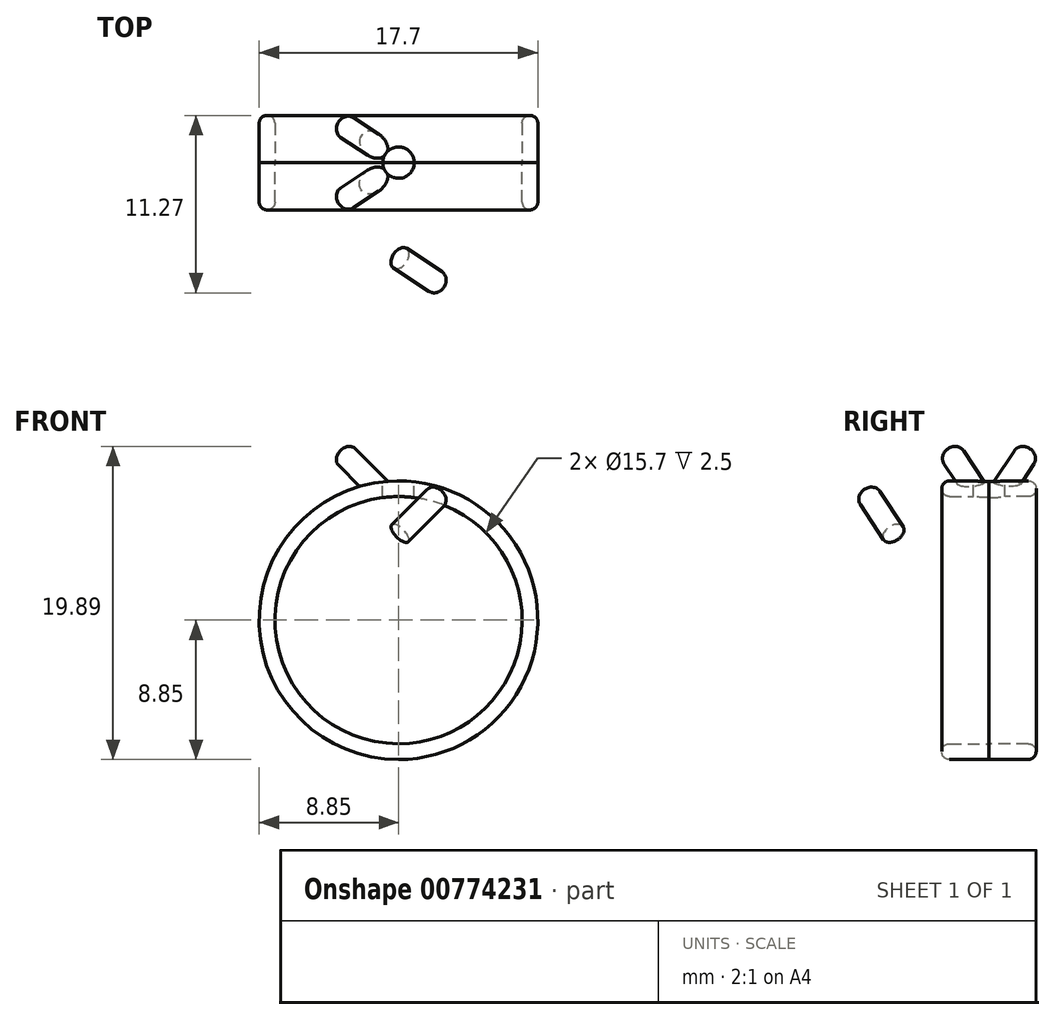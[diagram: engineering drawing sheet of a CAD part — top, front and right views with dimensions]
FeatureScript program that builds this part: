
annotation { "Feature Type Name" : "Feature", "Feature Type Description" : "" }
export const myFeature = defineFeature(function(context is Context, id is Id, definition is map)
    precondition{}
    {
        {
            var Q0;
            Q0=qCreatedBy(makeId("Front.planeOp"),FACE);
            var sketch = newSketch(context, id + "F0", { "sketchPlane" : qUnion([Q0])});
            skCircle(sketch, "E0", {"center": v(0, 0) * mm, "radius": 7.85 * mm});
            skCircle(sketch, "E1", {"center": v(0, 0) * mm, "radius": 8.85 * mm});
            skSolve(sketch);
        }
        {
            var Q0;
            Q0 = qSketchRegion(id + "F0", true);
            extrude(context, id + "F1", {"entities" : qUnion([Q0]), "depth" : 3 * mm, "offsetDistance" : 25 * mm});
        }
        {
            var Q0;
            Q0=makeQuery(id+"F1.opExtrude","CAP_FACE",FACE,{"disambiguationData":[OSD([sQuery(id+"F0.wireOp",EDGE,"E0"),sQuery(id+"F0.wireOp",EDGE,"E1")])],"isStart":false});
            cPlane(context, id + "F2", {"entities" : qUnion([Q0]), "cplaneType" : CPlaneType.OFFSET, "offset" : 2.25 * mm, "oppositeDirection" : true, "width" : 150 * mm, "height" : 150 * mm});
        }
        {
            var Q0;
            Q0=qCreatedBy(id+"F2.planeOp",FACE);
            var sketch = newSketch(context, id + "F3", { "sketchPlane" : qUnion([Q0])});
            skLineSegment(sketch, "E2", {"start": v(0, 15) * mm, "end": v(0, -15.53) * mm, "construction": true});
            skLineSegment(sketch, "E3", {"start": v(1, 8.09) * mm, "end": v(1, 8.1) * mm});
            skLineSegment(sketch, "E4", {"start": v(-1, 8.09) * mm, "end": v(-1, 8.1) * mm});
            skSolve(sketch);
        }
        {
            var Q0;
            Q0=sQuery(id+"F3.wireOp",EDGE,"E3");
            cPlane(context, id + "F4", {"entities" : qUnion([Q0]), "cplaneType" : CPlaneType.LINE_ANGLE, "offset" : 25 * mm, "angle" : 90 * degree, "oppositeDirection" : true, "width" : 150 * mm, "height" : 150 * mm});
        }
        {
            var Q0;
            Q0=sQuery(id+"F3.wireOp",EDGE,"E4");
            cPlane(context, id + "F5", {"entities" : qUnion([Q0]), "cplaneType" : CPlaneType.LINE_ANGLE, "offset" : 25 * mm, "angle" : 90 * degree, "width" : 150 * mm, "height" : 150 * mm});
        }
        {
            var Q0;
            Q0=qCreatedBy(id+"F4.planeOp",FACE);
            var sketch = newSketch(context, id + "F6", { "sketchPlane" : qUnion([Q0])});
            skLineSegment(sketch, "E5", {"start": v(-0.75, 6.44) * mm, "end": v(-0.75, 6.45) * mm});
            skLineSegment(sketch, "E6", {"start": v(-0.75, 6.45) * mm, "end": v(-2.44, 10.07) * mm});
            skSolve(sketch);
        }
        {
            var Q0;
            Q0=qCreatedBy(id+"F5.planeOp",FACE);
            var sketch = newSketch(context, id + "F7", { "sketchPlane" : qUnion([Q0])});
            skLineSegment(sketch, "E7", {"start": v(-0.75, 6.44) * mm, "end": v(-0.75, 6.45) * mm});
            skLineSegment(sketch, "E8", {"start": v(-0.75, 6.45) * mm, "end": v(-2.44, 10.07) * mm});
            skSolve(sketch);
        }
        {
            var Q0;
            Q0=sQuery(id+"F6.wireOp",VERTEX,"E6.end");
            var Q1;
            Q1=sQuery(id+"F6.wireOp",EDGE,"E6");
            cPlane(context, id + "F8", {"entities" : qUnion([Q0, Q1]), "cplaneType" : CPlaneType.LINE_POINT, "offset" : 25 * mm, "width" : 150 * mm, "height" : 150 * mm});
        }
        {
            var Q0;
            Q0=sQuery(id+"F7.wireOp",VERTEX,"E8.end");
            var Q1;
            Q1=sQuery(id+"F7.wireOp",EDGE,"E8");
            cPlane(context, id + "F9", {"entities" : qUnion([Q0, Q1]), "cplaneType" : CPlaneType.LINE_POINT, "offset" : 25 * mm, "width" : 150 * mm, "height" : 150 * mm});
        }
        {
            var Q0;
            Q0=qCreatedBy(id+"F8.planeOp",FACE);
            var sketch = newSketch(context, id + "F10", { "sketchPlane" : qUnion([Q0])});
            skCircle(sketch, "E9", {"center": v(-3.82, 3.83) * mm, "radius": 0.75 * mm});
            skSolve(sketch);
        }
        {
            var Q0;
            Q0=qCreatedBy(id+"F9.planeOp",FACE);
            var sketch = newSketch(context, id + "F11", { "sketchPlane" : qUnion([Q0])});
            skCircle(sketch, "E10", {"center": v(-2.04, 5.01) * mm, "radius": 0.75 * mm});
            skSolve(sketch);
        }
        {
            var Q0;
            Q0=makeQuery(id+"F10.imprint","IMPRINT",FACE,{"disambiguationData":[TD([[makeQuery(id+"F10.imprint","IMPRINT",EDGE,{"derivedFrom":sQuery(id+"F10.wireOp",EDGE,"E9")}),1.0]])]});
            var Q1;
            Q1=sQuery(id+"F6.wireOp",EDGE,"E6");
            sweep(context, id + "F12", {"operationType" : NewBodyOperationType.ADD, "profiles" : qUnion([Q0]), "path" : qUnion([Q1])});
        }
        {
            var Q0;
            Q0=makeQuery(id+"F11.imprint","IMPRINT",FACE,{"disambiguationData":[TD([[makeQuery(id+"F11.imprint","IMPRINT",EDGE,{"derivedFrom":sQuery(id+"F11.wireOp",EDGE,"E10")}),1.0]])]});
            var Q1;
            Q1=sQuery(id+"F7.wireOp",EDGE,"E8");
            sweep(context, id + "F13", {"operationType" : NewBodyOperationType.ADD, "profiles" : qUnion([Q0]), "path" : qUnion([Q1])});
        }
        {
            var Q0;
            Q0=qCreatedBy(makeId("Top.planeOp"),FACE);
            cPlane(context, id + "F14", {"entities" : qUnion([Q0]), "cplaneType" : CPlaneType.OFFSET, "offset" : 9 * mm, "width" : 150 * mm, "height" : 150 * mm});
        }
        {
            var Q0;
            Q0=qCreatedBy(id+"F14.planeOp",FACE);
            var sketch = newSketch(context, id + "F15", { "sketchPlane" : qUnion([Q0])});
            skCircle(sketch, "E11", {"center": v(0, 0) * mm, "radius": 1 * mm});
            skSolve(sketch);
        }
        {
            var Q0;
            Q0 = qSketchRegion(id + "F15", true);
            extrude(context, id + "F16", {"entities" : qUnion([Q0]), "operationType" : NewBodyOperationType.REMOVE, "oppositeDirection" : true, "depth" : 9 * mm, "offsetDistance" : 25 * mm});
        }
        {
            var Q0;
            Q0=makeQuery(id+"F1.opExtrude","SWEPT_BODY",BODY,{"disambiguationData":[OSD([sQuery(id+"F0.wireOp",EDGE,"E0"),sQuery(id+"F0.wireOp",EDGE,"E1")])]});
            var Q1;
            Q1=makeQuery(id+"F1.opExtrude","CAP_FACE",FACE,{"disambiguationData":[OSD([sQuery(id+"F0.wireOp",EDGE,"E0"),sQuery(id+"F0.wireOp",EDGE,"E1")])],"isStart":true});
            mirror(context, id + "F17", {"operationType" : NewBodyOperationType.ADD, "entities" : qUnion([Q0]), "mirrorPlane" : qUnion([Q1])});
        }
        {
            var Q0;
            Q0=makeQuery(id+"F1.opExtrude","CAP_FACE",FACE,{"disambiguationData":[OSD([sQuery(id+"F0.wireOp",EDGE,"E0"),sQuery(id+"F0.wireOp",EDGE,"E1")])],"isStart":false});
            var sketch = newSketch(context, id + "F18", { "sketchPlane" : qUnion([Q0])});
            skCircle(sketch, "E12", {"center": v(0, 0) * mm, "radius": 7.85 * mm});
            skSolve(sketch);
        }
        {
            var Q0;
            Q0 = qSketchRegion(id + "F18", true);
            extrude(context, id + "F19", {"entities" : qUnion([Q0]), "operationType" : NewBodyOperationType.REMOVE, "oppositeDirection" : true, "depth" : 25 * mm, "offsetDistance" : 25 * mm});
        }
        {
            var Q0;
            Q0=makeQuery(id+"F1.opExtrude","CAP_FACE",FACE,{"disambiguationData":[OSD([sQuery(id+"F0.wireOp",EDGE,"E0"),sQuery(id+"F0.wireOp",EDGE,"E1")])],"isStart":false});
            var Q1;
            Q1=makeQuery(id+"F17.opPattern","COPY",FACE,{"derivedFrom":makeQuery(id+"F1.opExtrude","CAP_FACE",FACE,{"disambiguationData":[OSD([sQuery(id+"F0.wireOp",EDGE,"E0"),sQuery(id+"F0.wireOp",EDGE,"E1")])],"isStart":false}),"instanceName":"1"});
            var Q2;
            Q2=makeQuery(id+"F17.opPattern","COPY",FACE,{"derivedFrom":makeQuery(id+"F12.opSweep","CAP_FACE",FACE,{"disambiguationData":[OSD([sQuery(id+"F6.wireOp",VERTEX,"E6.end"),sQuery(id+"F10.wireOp",EDGE,"E9")])],"isStart":true}),"instanceName":"1"});
            var Q3;
            Q3=makeQuery(id+"F12.opSweep","CAP_FACE",FACE,{"disambiguationData":[OSD([sQuery(id+"F6.wireOp",VERTEX,"E6.end"),sQuery(id+"F10.wireOp",EDGE,"E9")])],"isStart":true});
            var Q4;
            Q4=makeQuery(id+"F13.opSweep","CAP_FACE",FACE,{"disambiguationData":[OSD([sQuery(id+"F7.wireOp",VERTEX,"E8.end"),sQuery(id+"F11.wireOp",EDGE,"E10")])],"isStart":true});
            var Q5;
            Q5=makeQuery(id+"F17.opPattern","COPY",FACE,{"derivedFrom":makeQuery(id+"F13.opSweep","CAP_FACE",FACE,{"disambiguationData":[OSD([sQuery(id+"F7.wireOp",VERTEX,"E8.end"),sQuery(id+"F11.wireOp",EDGE,"E10")])],"isStart":true}),"instanceName":"1"});
            fillet(context, id + "F20", {"entities" : qUnion([Q0, Q1, Q2, Q3, Q4, Q5]), "tangentPropagation" : true, "radius" : .5 * mm, "defaultsChanged" : false, "vertexSettings" : [], "allowEdgeOverflow" : false});
        }
    });
